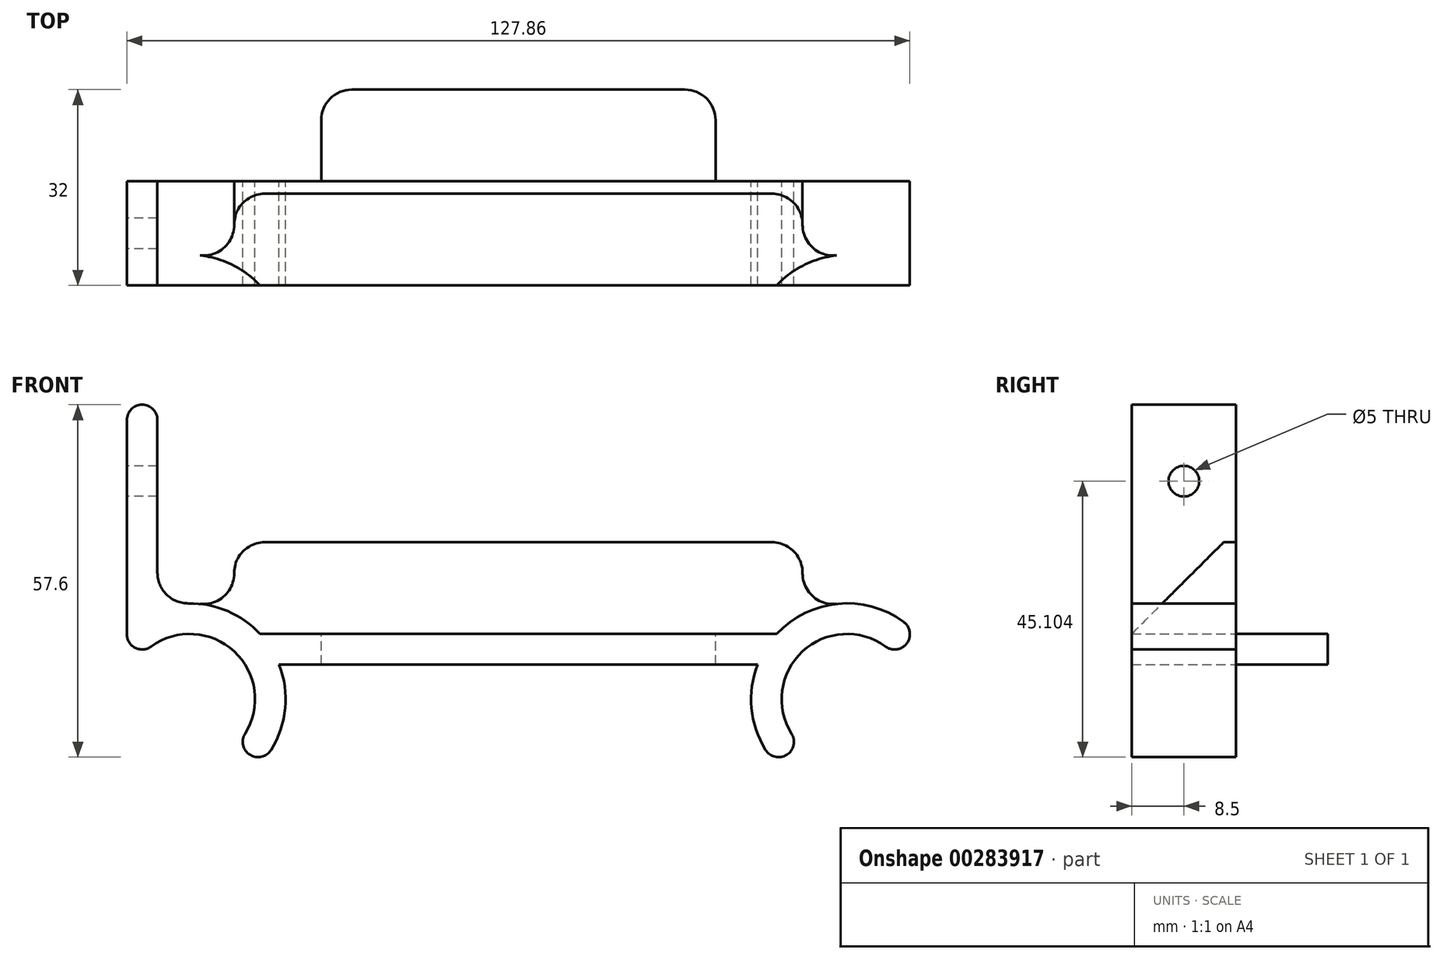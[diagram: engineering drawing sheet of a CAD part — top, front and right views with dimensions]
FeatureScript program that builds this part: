
annotation { "Feature Type Name" : "Feature", "Feature Type Description" : "" }
export const myFeature = defineFeature(function(context is Context, id is Id, definition is map)
    precondition{}
    {
        {
            var Q0;
            Q0=qCreatedBy(makeId("Front.planeOp"),FACE);
            var sketch = newSketch(context, id + "F0", { "sketchPlane" : qUnion([Q0])});
            skLineSegment(sketch, "E0", {"start": v(0, 0) * mm, "end": v(0, 38.7) * mm, "construction": true});
            skLineSegment(sketch, "E1", {"start": v(-43, 0) * mm, "end": v(43, 0) * mm, "construction": true});
            skCircle(sketch, "E2", {"center": v(53.67, 0) * mm, "radius": 10.67 * mm, "construction": true});
            skCircle(sketch, "E3", {"center": v(53.67, 0) * mm, "radius": 15.67 * mm, "construction": true});
            skLineSegment(sketch, "E4", {"start": v(53.67, 0) * mm, "end": v(53.67, 10.67) * mm, "construction": true});
            skLineSegment(sketch, "E5", {"start": v(53.67, 10.67) * mm, "end": v(0, 10.67) * mm, "construction": true});
            skArc(sketch, "E6", {"start": v(42.2, -10.67) * mm, "mid": v(38.28, -2.95) * mm, "end": v(39.06, 5.67) * mm});
            skArc(sketch, "E7", {"start": v(45.85, -7.26) * mm, "mid": v(46.4, 7.81) * mm, "end": v(61.48, 7.26) * mm});
            skLineSegment(sketch, "E8", {"start": v(53.67, 0) * mm, "end": v(53.67, -10.67) * mm, "construction": true});
            skLineSegment(sketch, "E9", {"start": v(42.2, -10.67) * mm, "end": v(65.14, 10.67) * mm, "construction": true});
            skLineSegment(sketch, "E10", {"start": v(42.2, -10.67) * mm, "end": v(45.85, -7.26) * mm});
            skLineSegment(sketch, "E11", {"start": v(61.48, 7.26) * mm, "end": v(65.14, 10.67) * mm});
            skArc(sketch, "E12", {"start": v(42.2, 10.67) * mm, "mid": v(53.67, 15.67) * mm, "end": v(65.14, 10.67) * mm});
            skLineSegment(sketch, "E13.MirrorCS", {"start": v(-42.2, -10.67) * mm, "end": v(-45.85, -7.26) * mm});
            skLineSegment(sketch, "E14.MirrorCS", {"start": v(-61.48, 7.26) * mm, "end": v(-65.14, 10.67) * mm});
            skArc(sketch, "E15.MirrorCS", {"start": v(-45.85, -7.26) * mm, "mid": v(-46.4, 7.81) * mm, "end": v(-61.48, 7.26) * mm});
            skArc(sketch, "E16.MirrorCS", {"start": v(-42.2, 10.67) * mm, "mid": v(-53.67, 15.67) * mm, "end": v(-65.14, 10.67) * mm});
            skArc(sketch, "E17.MirrorCS", {"start": v(-42.2, -10.67) * mm, "mid": v(-38.28, -2.95) * mm, "end": v(-39.06, 5.67) * mm});
            skLineSegment(sketch, "E18", {"start": v(-42.2, 10.67) * mm, "end": v(42.2, 10.67) * mm});
            skLineSegment(sketch, "E19", {"start": v(-39.06, 5.67) * mm, "end": v(39.06, 5.67) * mm});
            skSolve(sketch);
        }
        {
            var Q0;
            Q0 = qSketchRegion(id + "F0", true);
            extrude(context, id + "F1", {"entities" : qUnion([Q0]), "depth" : 17 * mm});
        }
        {
            var Q0;
            Q0=makeQuery(id+"F1.opExtrude","CAP_FACE",FACE,{"disambiguationData":[OSD([sQuery(id+"F0.wireOp",EDGE,"E6"),sQuery(id+"F0.wireOp",EDGE,"E7"),sQuery(id+"F0.wireOp",EDGE,"E10"),sQuery(id+"F0.wireOp",EDGE,"E11"),sQuery(id+"F0.wireOp",EDGE,"E12"),sQuery(id+"F0.wireOp",EDGE,"E13.MirrorCS"),sQuery(id+"F0.wireOp",EDGE,"E14.MirrorCS"),sQuery(id+"F0.wireOp",EDGE,"E15.MirrorCS"),sQuery(id+"F0.wireOp",EDGE,"E16.MirrorCS"),sQuery(id+"F0.wireOp",EDGE,"E17.MirrorCS"),sQuery(id+"F0.wireOp",EDGE,"E18"),sQuery(id+"F0.wireOp",EDGE,"E19")])],"isStart":true});
            var sketch = newSketch(context, id + "F2", { "sketchPlane" : qUnion([Q0])});
            skLineSegment(sketch, "E20.bottom", {"start": v(-46.4, 7.81) * mm, "end": v(46.4, 7.81) * mm});
            skLineSegment(sketch, "E20.top", {"start": v(-46.4, 25.67) * mm, "end": v(46.4, 25.67) * mm});
            skLineSegment(sketch, "E20.left", {"start": v(-46.4, 7.81) * mm, "end": v(-46.4, 25.67) * mm});
            skLineSegment(sketch, "E20.right", {"start": v(46.4, 7.81) * mm, "end": v(46.4, 25.67) * mm});
            skSolve(sketch);
        }
        {
            var Q0;
            Q0 = qSketchRegion(id + "F2", true);
            extrude(context, id + "F3", {"entities" : qUnion([Q0]), "operationType" : NewBodyOperationType.ADD, "oppositeDirection" : true, "depth" : 2 * mm});
        }
        {
            var Q0;
            Q0=makeQuery(id+"F3.boolean.opBoolean","MERGE",FACE,{"derivedFrom":[makeQuery(id+"F1.opExtrude","CAP_FACE",FACE,{"disambiguationData":[OSD([sQuery(id+"F0.wireOp",EDGE,"E6"),sQuery(id+"F0.wireOp",EDGE,"E7"),sQuery(id+"F0.wireOp",EDGE,"E10"),sQuery(id+"F0.wireOp",EDGE,"E11"),sQuery(id+"F0.wireOp",EDGE,"E12"),sQuery(id+"F0.wireOp",EDGE,"E13.MirrorCS"),sQuery(id+"F0.wireOp",EDGE,"E14.MirrorCS"),sQuery(id+"F0.wireOp",EDGE,"E15.MirrorCS"),sQuery(id+"F0.wireOp",EDGE,"E16.MirrorCS"),sQuery(id+"F0.wireOp",EDGE,"E17.MirrorCS"),sQuery(id+"F0.wireOp",EDGE,"E18"),sQuery(id+"F0.wireOp",EDGE,"E19")])],"isStart":true}),makeQuery(id+"F3.opExtrude","CAP_FACE",FACE,{"disambiguationData":[OSD([sQuery(id+"F2.wireOp",EDGE,"E20.bottom"),sQuery(id+"F2.wireOp",EDGE,"E20.top"),sQuery(id+"F2.wireOp",EDGE,"E20.left"),sQuery(id+"F2.wireOp",EDGE,"E20.right")])],"isStart":true})]});
            var sketch = newSketch(context, id + "F4", { "sketchPlane" : qUnion([Q0])});
            skLineSegment(sketch, "E21.0", {"start": v(-42.2, 10.67) * mm, "end": v(42.2, 10.67) * mm, "construction": true});
            skLineSegment(sketch, "E22.bottom", {"start": v(-32.2, 5.67) * mm, "end": v(32.2, 5.67) * mm});
            skLineSegment(sketch, "E22.top", {"start": v(-32.2, 10.67) * mm, "end": v(32.2, 10.67) * mm});
            skLineSegment(sketch, "E22.left", {"start": v(-32.2, 5.67) * mm, "end": v(-32.2, 10.67) * mm});
            skLineSegment(sketch, "E22.right", {"start": v(32.2, 5.67) * mm, "end": v(32.2, 10.67) * mm});
            skSolve(sketch);
        }
        {
            var Q0;
            Q0 = qSketchRegion(id + "F4", true);
            extrude(context, id + "F5", {"entities" : qUnion([Q0]), "operationType" : NewBodyOperationType.ADD, "depth" : 15 * mm});
        }
        {
            var Q0;
            Q0=makeQuery(id+"F1.opExtrude","SWEPT_EDGE",EDGE,{"disambiguationData":[OSD([sQuery(id+"F0.wireOp",EDGE,"E7"),sQuery(id+"F0.wireOp",EDGE,"E10")])]});
            var Q1;
            Q1=makeQuery(id+"F1.opExtrude","SWEPT_EDGE",EDGE,{"disambiguationData":[OSD([sQuery(id+"F0.wireOp",EDGE,"E6"),sQuery(id+"F0.wireOp",EDGE,"E10")])]});
            var Q2;
            Q2=makeQuery(id+"F1.opExtrude","SWEPT_EDGE",EDGE,{"disambiguationData":[OSD([sQuery(id+"F0.wireOp",EDGE,"E11"),sQuery(id+"F0.wireOp",EDGE,"E12")])]});
            var Q3;
            Q3=makeQuery(id+"F1.opExtrude","SWEPT_EDGE",EDGE,{"disambiguationData":[OSD([sQuery(id+"F0.wireOp",EDGE,"E7"),sQuery(id+"F0.wireOp",EDGE,"E11")])]});
            var Q4;
            Q4=makeQuery(id+"F1.opExtrude","SWEPT_EDGE",EDGE,{"disambiguationData":[OSD([sQuery(id+"F0.wireOp",EDGE,"E13.MirrorCS"),sQuery(id+"F0.wireOp",EDGE,"E17.MirrorCS")])]});
            var Q5;
            Q5=makeQuery(id+"F1.opExtrude","SWEPT_EDGE",EDGE,{"disambiguationData":[OSD([sQuery(id+"F0.wireOp",EDGE,"E13.MirrorCS"),sQuery(id+"F0.wireOp",EDGE,"E15.MirrorCS")])]});
            var Q6;
            Q6=makeQuery(id+"F1.opExtrude","SWEPT_EDGE",EDGE,{"disambiguationData":[OSD([sQuery(id+"F0.wireOp",EDGE,"E14.MirrorCS"),sQuery(id+"F0.wireOp",EDGE,"E15.MirrorCS")])]});
            var Q7;
            Q7=makeQuery(id+"F1.opExtrude","SWEPT_EDGE",EDGE,{"disambiguationData":[OSD([sQuery(id+"F0.wireOp",EDGE,"E14.MirrorCS"),sQuery(id+"F0.wireOp",EDGE,"E16.MirrorCS")])]});
            fillet(context, id + "F6", {"entities" : qUnion([Q0, Q1, Q2, Q3, Q4, Q5, Q6, Q7]), "radius" : 2.5 * mm, "tangentPropagation" : true, "allowEdgeOverflow" : false});
        }
        {
            var Q0;
            Q0=makeQuery(id+"F3.opExtrude","SWEPT_EDGE",EDGE,{"disambiguationData":[OSD([sQuery(id+"F2.wireOp",EDGE,"E20.top"),sQuery(id+"F2.wireOp",EDGE,"E20.left")])]});
            var Q1;
            Q1=makeQuery(id+"F3.boolean.opBoolean","INTERSECT",EDGE,{"derivedFrom":[makeQuery(id+"F1.opExtrude","SWEPT_FACE",FACE,{"disambiguationData":[OSD([sQuery(id+"F0.wireOp",EDGE,"E12")])]}),makeQuery(id+"F3.opExtrude","SWEPT_FACE",FACE,{"disambiguationData":[OSD([sQuery(id+"F2.wireOp",EDGE,"E20.left")])]})]});
            var Q2;
            Q2=makeQuery(id+"F3.opExtrude","SWEPT_EDGE",EDGE,{"disambiguationData":[OSD([sQuery(id+"F2.wireOp",EDGE,"E20.top"),sQuery(id+"F2.wireOp",EDGE,"E20.right")])]});
            var Q3;
            Q3=makeQuery(id+"F3.boolean.opBoolean","INTERSECT",EDGE,{"derivedFrom":[makeQuery(id+"F1.opExtrude","SWEPT_FACE",FACE,{"disambiguationData":[OSD([sQuery(id+"F0.wireOp",EDGE,"E16.MirrorCS")])]}),makeQuery(id+"F3.opExtrude","SWEPT_FACE",FACE,{"disambiguationData":[OSD([sQuery(id+"F2.wireOp",EDGE,"E20.right")])]})]});
            var Q4;
            Q4=makeQuery(id+"F5.opExtrude","CAP_EDGE",EDGE,{"disambiguationData":[OSD([sQuery(id+"F4.wireOp",EDGE,"E22.right")])],"isStart":true});
            var Q5;
            Q5=makeQuery(id+"F5.opExtrude","CAP_EDGE",EDGE,{"disambiguationData":[OSD([sQuery(id+"F4.wireOp",EDGE,"E22.left")])],"isStart":true});
            var Q6;
            Q6=makeQuery(id+"F5.opExtrude","CAP_EDGE",EDGE,{"disambiguationData":[OSD([sQuery(id+"F4.wireOp",EDGE,"E22.left")])],"isStart":false});
            var Q7;
            Q7=makeQuery(id+"F5.opExtrude","CAP_EDGE",EDGE,{"disambiguationData":[OSD([sQuery(id+"F4.wireOp",EDGE,"E22.right")])],"isStart":false});
            fillet(context, id + "F7", {"entities" : qUnion([Q0, Q1, Q2, Q3, Q4, Q5, Q6, Q7]), "radius" : 5 * mm, "tangentPropagation" : true, "allowEdgeOverflow" : false});
        }
        {
            var Q0;
            Q0=makeQuery(id+"F3.boolean.opBoolean","INTERSECT",EDGE,{"derivedFrom":[makeQuery(id+"F1.opExtrude","SWEPT_FACE",FACE,{"disambiguationData":[OSD([sQuery(id+"F0.wireOp",EDGE,"E18")])]}),makeQuery(id+"F3.opExtrude","CAP_FACE",FACE,{"disambiguationData":[OSD([sQuery(id+"F2.wireOp",EDGE,"E20.bottom"),sQuery(id+"F2.wireOp",EDGE,"E20.top"),sQuery(id+"F2.wireOp",EDGE,"E20.left"),sQuery(id+"F2.wireOp",EDGE,"E20.right")])],"isStart":false})]});
            chamfer(context, id + "F8", {"entities" : qUnion([Q0]), "chamferType" : ChamferType.TWO_OFFSETS, "width1" : 15 * mm, "oppositeDirection" : false, "width2" : 15 * mm, "tangentPropagation" : true});
        }
        {
            var Q0;
            Q0=makeQuery(id+"F1.opExtrude","CAP_FACE",FACE,{"disambiguationData":[OSD([sQuery(id+"F0.wireOp",EDGE,"E6"),sQuery(id+"F0.wireOp",EDGE,"E7"),sQuery(id+"F0.wireOp",EDGE,"E10"),sQuery(id+"F0.wireOp",EDGE,"E11"),sQuery(id+"F0.wireOp",EDGE,"E12"),sQuery(id+"F0.wireOp",EDGE,"E13.MirrorCS"),sQuery(id+"F0.wireOp",EDGE,"E14.MirrorCS"),sQuery(id+"F0.wireOp",EDGE,"E15.MirrorCS"),sQuery(id+"F0.wireOp",EDGE,"E16.MirrorCS"),sQuery(id+"F0.wireOp",EDGE,"E17.MirrorCS"),sQuery(id+"F0.wireOp",EDGE,"E18"),sQuery(id+"F0.wireOp",EDGE,"E19")])],"isStart":false});
            var sketch = newSketch(context, id + "F9", { "sketchPlane" : qUnion([Q0])});
            skArc(sketch, "E23.0", {"start": v(-63.93, 10.63) * mm, "mid": v(-62.57, 8.4) * mm, "end": v(-59.96, 8.61) * mm});
            skArc(sketch, "E24.0", {"start": v(-58.93, 9.28) * mm, "mid": v(-59.46, 8.96) * mm, "end": v(-59.96, 8.61) * mm});
            skLineSegment(sketch, "E25", {"start": v(-58.93, 9.28) * mm, "end": v(-58.93, 45.63) * mm});
            skLineSegment(sketch, "E26", {"start": v(-61.43, 10.63) * mm, "end": v(-63.93, 10.63) * mm, "construction": true});
            skLineSegment(sketch, "E27", {"start": v(-63.93, 10.63) * mm, "end": v(-63.93, 45.63) * mm});
            skArc(sketch, "E28", {"start": v(-58.93, 45.63) * mm, "mid": v(-61.43, 48.13) * mm, "end": v(-63.93, 45.63) * mm});
            skPoint(sketch, "E29.orphan", {"position": v(-62.9, 12.65) * mm});
            skPoint(sketch, "E30.orphan", {"position": v(-44.62, -5.65) * mm});
            skSolve(sketch);
        }
        {
            var Q0;
            Q0 = qSketchRegion(id + "F9", true);
            var Q1;
            Q1=makeQuery(id+"F3.boolean.opBoolean","MERGE",FACE,{"derivedFrom":[makeQuery(id+"F1.opExtrude","CAP_FACE",FACE,{"disambiguationData":[OSD([sQuery(id+"F0.wireOp",EDGE,"E6"),sQuery(id+"F0.wireOp",EDGE,"E7"),sQuery(id+"F0.wireOp",EDGE,"E10"),sQuery(id+"F0.wireOp",EDGE,"E11"),sQuery(id+"F0.wireOp",EDGE,"E12"),sQuery(id+"F0.wireOp",EDGE,"E13.MirrorCS"),sQuery(id+"F0.wireOp",EDGE,"E14.MirrorCS"),sQuery(id+"F0.wireOp",EDGE,"E15.MirrorCS"),sQuery(id+"F0.wireOp",EDGE,"E16.MirrorCS"),sQuery(id+"F0.wireOp",EDGE,"E17.MirrorCS"),sQuery(id+"F0.wireOp",EDGE,"E18"),sQuery(id+"F0.wireOp",EDGE,"E19")])],"isStart":true}),makeQuery(id+"F3.opExtrude","CAP_FACE",FACE,{"disambiguationData":[OSD([sQuery(id+"F2.wireOp",EDGE,"E20.bottom"),sQuery(id+"F2.wireOp",EDGE,"E20.top"),sQuery(id+"F2.wireOp",EDGE,"E20.left"),sQuery(id+"F2.wireOp",EDGE,"E20.right")])],"isStart":true})]});
            extrude(context, id + "F10", {"entities" : qUnion([Q0]), "operationType" : NewBodyOperationType.ADD, "endBound" : BoundingType.UP_TO_SURFACE, "oppositeDirection" : true, "endBoundEntityFace" : qUnion([Q1]), "depth" : 25 * mm});
        }
        {
            var Q0;
            Q0=makeQuery(id+"F10.boolean.opBoolean","INTERSECT",EDGE,{"derivedFrom":[makeQuery(id+"F1.opExtrude","SWEPT_FACE",FACE,{"disambiguationData":[OSD([sQuery(id+"F0.wireOp",EDGE,"E16.MirrorCS")])]}),makeQuery(id+"F10.opExtrude","SWEPT_FACE",FACE,{"disambiguationData":[OSD([sQuery(id+"F9.wireOp",EDGE,"E25")])]})]});
            fillet(context, id + "F11", {"entities" : qUnion([Q0]), "radius" : 5 * mm, "tangentPropagation" : true, "allowEdgeOverflow" : false});
        }
        {
            var Q0;
            Q0=makeQuery(id+"F10.opExtrude","SWEPT_FACE",FACE,{"disambiguationData":[OSD([sQuery(id+"F9.wireOp",EDGE,"E27")])]});
            var sketch = newSketch(context, id + "F12", { "sketchPlane" : qUnion([Q0])});
            skLineSegment(sketch, "E31", {"start": v(8.5, 45.63) * mm, "end": v(8.5, 35.63) * mm, "construction": true});
            skCircle(sketch, "E32", {"center": v(8.5, 35.63) * mm, "radius": 2.5 * mm});
            skSolve(sketch);
        }
        {
            var Q0;
            Q0 = qSketchRegion(id + "F12", true);
            extrude(context, id + "F13", {"entities" : qUnion([Q0]), "operationType" : NewBodyOperationType.REMOVE, "endBound" : BoundingType.UP_TO_NEXT, "oppositeDirection" : true, "depth" : 25 * mm});
        }
    });
